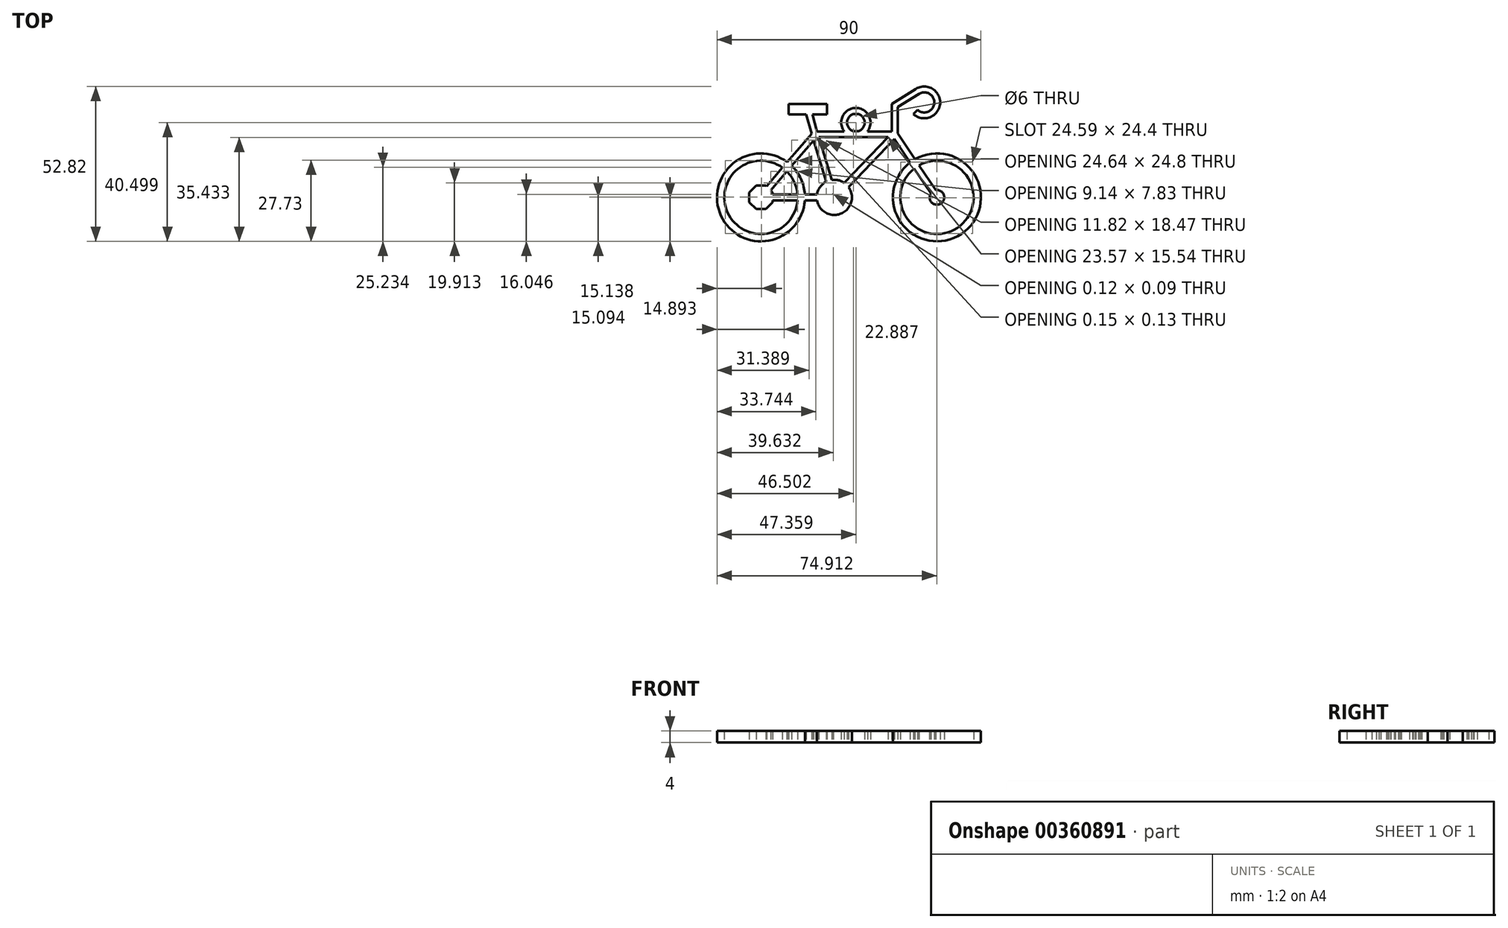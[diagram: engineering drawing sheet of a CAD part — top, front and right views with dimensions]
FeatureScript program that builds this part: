
annotation { "Feature Type Name" : "Feature", "Feature Type Description" : "" }
export const myFeature = defineFeature(function(context is Context, id is Id, definition is map)
    precondition{}
    {
        {
            var Q0;
            Q0=qCreatedBy(makeId("Top.planeOp"),FACE);
            var sketch = newSketch(context, id + "F0", { "sketchPlane" : qUnion([Q0])});
            skCircle(sketch, "E0", {"center": v(0, 0) * mm, "radius": 6 * mm});
            skCircle(sketch, "E1", {"center": v(35, 0) * mm, "radius": 2.5 * mm});
            skCircle(sketch, "E2", {"center": v(35, 0) * mm, "radius": 12.5 * mm});
            skCircle(sketch, "E3", {"center": v(35, 0) * mm, "radius": 15 * mm});
            skCircle(sketch, "E4", {"center": v(-25, 0) * mm, "radius": 12.5 * mm});
            skCircle(sketch, "E5", {"center": v(-25, 0) * mm, "radius": 15 * mm});
            skArc(sketch, "E6", {"start": v(28.35, 29.88) * mm, "mid": v(34.07, 32.08) * mm, "end": v(28.85, 35.3) * mm});
            skCircle(sketch, "E7.cCircle", {"center": v(-25, 0) * mm, "radius": 4 * mm, "construction": true});
            skLineSegment(sketch, "E7.0", {"start": v(-21, -1.66) * mm, "end": v(-23.34, -4) * mm});
            skLineSegment(sketch, "E7.1", {"start": v(-23.34, -4) * mm, "end": v(-26.66, -4) * mm});
            skLineSegment(sketch, "E7.2", {"start": v(-26.66, -4) * mm, "end": v(-29, -1.66) * mm});
            skLineSegment(sketch, "E7.3", {"start": v(-29, -1.66) * mm, "end": v(-29, 1.66) * mm});
            skLineSegment(sketch, "E7.4", {"start": v(-29, 1.66) * mm, "end": v(-26.66, 4) * mm});
            skLineSegment(sketch, "E7.5", {"start": v(-26.66, 4) * mm, "end": v(-23.34, 4) * mm});
            skLineSegment(sketch, "E7.6", {"start": v(-23.34, 4) * mm, "end": v(-21, 1.66) * mm});
            skLineSegment(sketch, "E7.7", {"start": v(-21, 1.66) * mm, "end": v(-21, -1.66) * mm});
            skPoint(sketch, "E7.0.midPoint", {"position": v(-22.17, -2.83) * mm});
            skLineSegment(sketch, "E8", {"start": v(0, 0) * mm, "end": v(-6.64, 21.5) * mm});
            skLineSegment(sketch, "E9", {"start": v(-6.64, 21.5) * mm, "end": v(-25, 0) * mm});
            skLineSegment(sketch, "E10", {"start": v(-6.64, 21.5) * mm, "end": v(20.63, 21.5) * mm});
            skLineSegment(sketch, "E11", {"start": v(20.63, 21.5) * mm, "end": v(35, 0) * mm});
            skLineSegment(sketch, "E12", {"start": v(20.63, 21.5) * mm, "end": v(0, 0) * mm});
            skLineSegment(sketch, "E13", {"start": v(-6.64, 21.5) * mm, "end": v(-9, 30.11) * mm});
            skLineSegment(sketch, "E14.bottom", {"start": v(-2.48, 28.35) * mm, "end": v(-15.52, 28.35) * mm});
            skLineSegment(sketch, "E14.top", {"start": v(-2.48, 31.87) * mm, "end": v(-15.52, 31.87) * mm});
            skLineSegment(sketch, "E14.left", {"start": v(-2.48, 28.35) * mm, "end": v(-2.48, 31.87) * mm});
            skLineSegment(sketch, "E14.right", {"start": v(-15.52, 28.35) * mm, "end": v(-15.52, 31.87) * mm});
            skPoint(sketch, "E14.middle", {"position": v(-9, 30.11) * mm});
            skLineSegment(sketch, "E15", {"start": v(20.63, 21.5) * mm, "end": v(20.63, 31.33) * mm});
            skLineSegment(sketch, "E16", {"start": v(20.63, 31.33) * mm, "end": v(28.64, 36.35) * mm});
            skArc(sketch, "E17.0", {"start": v(27, 28.4) * mm, "mid": v(35.76, 34.26) * mm, "end": v(25.28, 33.06) * mm});
            skLineSegment(sketch, "E18.0", {"start": v(19.63, 31.89) * mm, "end": v(28.1, 37.2) * mm});
            skLineSegment(sketch, "E18.1", {"start": v(19.63, 21.5) * mm, "end": v(19.63, 31.89) * mm});
            skLineSegment(sketch, "E19.0", {"start": v(19.8, 20.94) * mm, "end": v(33.87, -0.1) * mm});
            skLineSegment(sketch, "E20.0", {"start": v(19.91, 22.2) * mm, "end": v(-1.2, 0.19) * mm});
            skLineSegment(sketch, "E21.0", {"start": v(21.36, 20.8) * mm, "end": v(0.24, -1.2) * mm});
            skLineSegment(sketch, "E22.0", {"start": v(0.96, 0.3) * mm, "end": v(-5.69, 21.8) * mm});
            skLineSegment(sketch, "E23.0", {"start": v(-0.96, -0.3) * mm, "end": v(-7.6, 21.2) * mm});
            skLineSegment(sketch, "E24.0", {"start": v(-6.64, 20.5) * mm, "end": v(21.63, 20.5) * mm});
            skLineSegment(sketch, "E25.0", {"start": v(-6.64, 22.5) * mm, "end": v(21.63, 22.5) * mm});
            skLineSegment(sketch, "E26.0", {"start": v(-7.4, 22.15) * mm, "end": v(-25.76, 0.65) * mm});
            skLineSegment(sketch, "E27.0", {"start": v(-5.88, 20.85) * mm, "end": v(-24.24, -0.65) * mm});
            skLineSegment(sketch, "E28", {"start": v(-25, 0) * mm, "end": v(0, 0) * mm});
            skLineSegment(sketch, "E29.0", {"start": v(-25, -1) * mm, "end": v(0, -1) * mm});
            skLineSegment(sketch, "E30.0", {"start": v(-25, 1) * mm, "end": v(0, 1) * mm});
            skLineSegment(sketch, "E31.0", {"start": v(21.47, 22.05) * mm, "end": v(35.53, 1) * mm});
            skLineSegment(sketch, "E32.0", {"start": v(21.63, 30.78) * mm, "end": v(29.17, 35.5) * mm});
            skLineSegment(sketch, "E32.1", {"start": v(21.63, 21.5) * mm, "end": v(21.63, 30.78) * mm});
            skLineSegment(sketch, "E33.0", {"start": v(-5.68, 21.76) * mm, "end": v(-8.04, 30.37) * mm});
            skLineSegment(sketch, "E34.0", {"start": v(-7.6, 21.23) * mm, "end": v(-9.97, 29.85) * mm});
            skLineSegment(sketch, "E35", {"start": v(30.66, 32.4) * mm, "end": v(20.63, 21.5) * mm});
            skCircle(sketch, "E36", {"center": v(7.36, 25.5) * mm, "radius": 5 * mm});
            skCircle(sketch, "E37", {"center": v(7.36, 25.5) * mm, "radius": 3 * mm});
            skSolve(sketch);
        }
        {
            var Q0;
            Q0=makeQuery(id+"F0.imprint","IMPRINT",FACE,{"disambiguationData":[TD([[makeQuery(id+"F0.imprint","IMPRINT",EDGE,{"derivedFrom":sQuery(id+"F0.wireOp",EDGE,"E14.top")}),1.0]])]});
            var Q1;
            {var subQ3=sQuery(id+"F0.wireOp",EDGE,"E37");Q1=makeQuery(id+"F0.imprint","IMPRINT",FACE,{"disambiguationData":[TD([[makeQuery(id+"F0.imprint","IMPRINT",EDGE,{"derivedFrom":subQ3}),-1.0]])]});}
            var Q2;
            {var subQ0=sQuery(id+"F0.wireOp",EDGE,"E32.1");var subQ1=sQuery(id+"F0.wireOp",EDGE,"E25.0");var subQ2=makeQuery(id+"F0.imprint","INTERSECT",VERTEX,{"derivedFrom":[subQ1,subQ0]});Q2=makeQuery(id+"F0.imprint","IMPRINT",FACE,{"disambiguationData":[TD([[makeQuery(id+"F0.imprint","IMPRINT",EDGE,{"disambiguationData":[TD([[subQ2,1.0]])],"derivedFrom":subQ1}),1.0]])]});}
            var Q3;
            {var subQ0=sQuery(id+"F0.wireOp",EDGE,"E29.0");var subQ1=sQuery(id+"F0.wireOp",EDGE,"E0");var subQ2=makeQuery(id+"F0.imprint","INTERSECT",VERTEX,{"derivedFrom":[subQ1,subQ0]});Q3=makeQuery(id+"F0.imprint","IMPRINT",FACE,{"disambiguationData":[TD([[makeQuery(id+"F0.imprint","IMPRINT",EDGE,{"disambiguationData":[TD([[subQ2,1.0]])],"derivedFrom":subQ1}),-1.0]])]});}
            var Q4;
            {var subQ0=sQuery(id+"F0.wireOp",EDGE,"E31.0");var subQ1=sQuery(id+"F0.wireOp",EDGE,"E2");var subQ2=makeQuery(id+"F0.imprint","INTERSECT",VERTEX,{"derivedFrom":[subQ1,subQ0]});Q4=makeQuery(id+"F0.imprint","IMPRINT",FACE,{"disambiguationData":[TD([[makeQuery(id+"F0.imprint","IMPRINT",EDGE,{"disambiguationData":[TD([[subQ2,1.0]])],"derivedFrom":subQ1}),-1.0]])]});}
            var Q5;
            {var subQ0=sQuery(id+"F0.wireOp",EDGE,"E26.0");var subQ1=sQuery(id+"F0.wireOp",EDGE,"E4");var subQ2=makeQuery(id+"F0.imprint","INTERSECT",VERTEX,{"derivedFrom":[subQ1,subQ0]});Q5=makeQuery(id+"F0.imprint","IMPRINT",FACE,{"disambiguationData":[TD([[makeQuery(id+"F0.imprint","IMPRINT",EDGE,{"disambiguationData":[TD([[subQ2,-1.0]])],"derivedFrom":subQ1}),-1.0]])]});}
            var Q6;
            {var subQ4=sQuery(id+"F0.wireOp",EDGE,"E6");Q6=makeQuery(id+"F0.imprint","IMPRINT",FACE,{"disambiguationData":[TD([[makeQuery(id+"F0.imprint","IMPRINT",EDGE,{"derivedFrom":subQ4}),-1.0]])]});}
            var Q7;
            {var subQ1=sQuery(id+"F0.wireOp",EDGE,"E22.0");var subQ7=sQuery(id+"F0.wireOp",EDGE,"E10");var subQ8=makeQuery(id+"F0.imprint","INTERSECT",VERTEX,{"derivedFrom":[subQ7,subQ1]});Q7=makeQuery(id+"F0.imprint","IMPRINT",FACE,{"disambiguationData":[TD([[makeQuery(id+"F0.imprint","IMPRINT",EDGE,{"disambiguationData":[TD([[subQ8,-1.0]])],"derivedFrom":subQ7}),1.0]])]});}
            var Q8;
            {var subQ3=sQuery(id+"F0.wireOp",EDGE,"E16");var subQ5=sQuery(id+"F0.wireOp",EDGE,"E15");var subQ6=makeQuery(id+"F0.imprint","INTERSECT",VERTEX,{"derivedFrom":[subQ5,subQ3]});Q8=makeQuery(id+"F0.imprint","IMPRINT",FACE,{"disambiguationData":[TD([[makeQuery(id+"F0.imprint","IMPRINT",EDGE,{"disambiguationData":[TD([[subQ6,1.0]])],"derivedFrom":subQ5}),1.0]])]});}
            var Q9;
            {var subQ0=sQuery(id+"F0.wireOp",EDGE,"E21.0");var subQ1=sQuery(id+"F0.wireOp",EDGE,"E19.0");var subQ2=makeQuery(id+"F0.imprint","INTERSECT",VERTEX,{"derivedFrom":[subQ1,subQ0]});Q9=makeQuery(id+"F0.imprint","IMPRINT",FACE,{"disambiguationData":[TD([[makeQuery(id+"F0.imprint","IMPRINT",EDGE,{"disambiguationData":[TD([[subQ2,1.0]])],"derivedFrom":subQ1}),1.0]])]});}
            var Q10;
            {var subQ0=sQuery(id+"F0.wireOp",EDGE,"E21.0");var subQ6=sQuery(id+"F0.wireOp",EDGE,"E0");var subQ9=makeQuery(id+"F0.imprint","INTERSECT",VERTEX,{"derivedFrom":[subQ6,subQ0]});Q10=makeQuery(id+"F0.imprint","IMPRINT",FACE,{"disambiguationData":[TD([[makeQuery(id+"F0.imprint","IMPRINT",EDGE,{"disambiguationData":[TD([[subQ9,-1.0]])],"derivedFrom":subQ6}),-1.0]])]});}
            var Q11;
            {var subQ0=sQuery(id+"F0.wireOp",EDGE,"E11");var subQ1=sQuery(id+"F0.wireOp",EDGE,"E2");var subQ2=makeQuery(id+"F0.imprint","INTERSECT",VERTEX,{"derivedFrom":[subQ1,subQ0]});Q11=makeQuery(id+"F0.imprint","IMPRINT",FACE,{"disambiguationData":[TD([[makeQuery(id+"F0.imprint","IMPRINT",EDGE,{"disambiguationData":[TD([[subQ2,1.0]])],"derivedFrom":subQ1}),-1.0]])]});}
            var Q12;
            {var subQ0=sQuery(id+"F0.wireOp",EDGE,"E11");var subQ1=sQuery(id+"F0.wireOp",EDGE,"E2");var subQ2=makeQuery(id+"F0.imprint","INTERSECT",VERTEX,{"derivedFrom":[subQ1,subQ0]});Q12=makeQuery(id+"F0.imprint","IMPRINT",FACE,{"disambiguationData":[TD([[makeQuery(id+"F0.imprint","IMPRINT",EDGE,{"disambiguationData":[TD([[subQ2,-1.0]])],"derivedFrom":subQ1}),-1.0]])]});}
            var Q13;
            {var subQ1=sQuery(id+"F0.wireOp",EDGE,"E19.0");var subQ5=sQuery(id+"F0.wireOp",EDGE,"E3");var subQ6=makeQuery(id+"F0.imprint","INTERSECT",VERTEX,{"derivedFrom":[subQ5,subQ1]});Q13=makeQuery(id+"F0.imprint","IMPRINT",FACE,{"disambiguationData":[TD([[makeQuery(id+"F0.imprint","IMPRINT",EDGE,{"disambiguationData":[TD([[subQ6,1.0]])],"derivedFrom":subQ5}),-1.0]])]});}
            var Q14;
            {var subQ0=sQuery(id+"F0.wireOp",EDGE,"E9");var subQ1=sQuery(id+"F0.wireOp",EDGE,"E4");var subQ2=makeQuery(id+"F0.imprint","INTERSECT",VERTEX,{"derivedFrom":[subQ1,subQ0]});Q14=makeQuery(id+"F0.imprint","IMPRINT",FACE,{"disambiguationData":[TD([[makeQuery(id+"F0.imprint","IMPRINT",EDGE,{"disambiguationData":[TD([[subQ2,-1.0]])],"derivedFrom":subQ1}),-1.0]])]});}
            var Q15;
            {var subQ0=sQuery(id+"F0.wireOp",EDGE,"E28");var subQ1=sQuery(id+"F0.wireOp",EDGE,"E4");var subQ2=makeQuery(id+"F0.imprint","INTERSECT",VERTEX,{"derivedFrom":[subQ1,subQ0]});Q15=makeQuery(id+"F0.imprint","IMPRINT",FACE,{"disambiguationData":[TD([[makeQuery(id+"F0.imprint","IMPRINT",EDGE,{"disambiguationData":[TD([[subQ2,1.0]])],"derivedFrom":subQ1}),-1.0]])]});}
            var Q16;
            {var subQ0=sQuery(id+"F0.wireOp",EDGE,"E33.0");var subQ5=sQuery(id+"F0.wireOp",EDGE,"E14.bottom");var subQ6=makeQuery(id+"F0.imprint","INTERSECT",VERTEX,{"derivedFrom":[subQ5,subQ0]});Q16=makeQuery(id+"F0.imprint","IMPRINT",FACE,{"disambiguationData":[TD([[makeQuery(id+"F0.imprint","IMPRINT",EDGE,{"disambiguationData":[TD([[subQ6,-1.0]])],"derivedFrom":subQ5}),1.0]])]});}
            var Q17;
            {var subQ2=sQuery(id+"F0.wireOp",EDGE,"E36");var subQ5=sQuery(id+"F0.wireOp",EDGE,"E10");var subQ6=makeQuery(id+"F0.imprint","INTERSECT",VERTEX,{"disambiguationData":[OD(0.0)],"derivedFrom":[subQ5,subQ2]});Q17=makeQuery(id+"F0.imprint","IMPRINT",FACE,{"disambiguationData":[TD([[makeQuery(id+"F0.imprint","IMPRINT",EDGE,{"disambiguationData":[TD([[subQ6,-1.0]])],"derivedFrom":subQ5}),1.0]])]});}
            var Q18;
            {var subQ3=sQuery(id+"F0.wireOp",EDGE,"E36");var subQ7=sQuery(id+"F0.wireOp",EDGE,"E10");var subQ9=makeQuery(id+"F0.imprint","INTERSECT",VERTEX,{"disambiguationData":[OD(1.0)],"derivedFrom":[subQ7,subQ3]});Q18=makeQuery(id+"F0.imprint","IMPRINT",FACE,{"disambiguationData":[TD([[makeQuery(id+"F0.imprint","IMPRINT",EDGE,{"disambiguationData":[TD([[subQ9,-1.0]])],"derivedFrom":subQ7}),1.0]])]});}
            var Q19;
            {var subQ6=sQuery(id+"F0.wireOp",EDGE,"E5");var subQ8=sQuery(id+"F0.wireOp",EDGE,"E26.0");var subQ9=makeQuery(id+"F0.imprint","INTERSECT",VERTEX,{"derivedFrom":[subQ6,subQ8]});Q19=makeQuery(id+"F0.imprint","IMPRINT",FACE,{"disambiguationData":[TD([[makeQuery(id+"F0.imprint","IMPRINT",EDGE,{"disambiguationData":[TD([[subQ9,1.0]])],"derivedFrom":subQ6}),-1.0]])]});}
            var Q20;
            {var subQ0=sQuery(id+"F0.wireOp",EDGE,"E18.1");var subQ4=sQuery(id+"F0.wireOp",EDGE,"E10");var subQ5=makeQuery(id+"F0.imprint","INTERSECT",VERTEX,{"derivedFrom":[subQ4,subQ0]});Q20=makeQuery(id+"F0.imprint","IMPRINT",FACE,{"disambiguationData":[TD([[makeQuery(id+"F0.imprint","IMPRINT",EDGE,{"disambiguationData":[TD([[subQ5,-1.0]])],"derivedFrom":subQ0}),-1.0]])]});}
            var Q21;
            {var subQ1=sQuery(id+"F0.wireOp",EDGE,"E15");var subQ10=sQuery(id+"F0.wireOp",EDGE,"E16");var subQ12=makeQuery(id+"F0.imprint","INTERSECT",VERTEX,{"derivedFrom":[subQ1,subQ10]});Q21=makeQuery(id+"F0.imprint","IMPRINT",FACE,{"disambiguationData":[TD([[makeQuery(id+"F0.imprint","IMPRINT",EDGE,{"disambiguationData":[TD([[subQ12,1.0]])],"derivedFrom":subQ1}),-1.0]])]});}
            var Q22;
            {var subQ2=sQuery(id+"F0.wireOp",EDGE,"E0");var subQ4=makeQuery(id+"F0.imprint","INTERSECT",VERTEX,{"derivedFrom":[subQ2,sQuery(id+"F0.wireOp",EDGE,"E21.0")]});Q22=makeQuery(id+"F0.imprint","IMPRINT",FACE,{"disambiguationData":[TD([[makeQuery(id+"F0.imprint","IMPRINT",EDGE,{"disambiguationData":[TD([[subQ4,-1.0]])],"derivedFrom":subQ2}),1.0]])]});}
            var Q23;
            {var subQ9=sQuery(id+"F0.wireOp",EDGE,"E3");var subQ11=sQuery(id+"F0.wireOp",EDGE,"E31.0");var subQ13=makeQuery(id+"F0.imprint","INTERSECT",VERTEX,{"derivedFrom":[subQ9,subQ11]});Q23=makeQuery(id+"F0.imprint","IMPRINT",FACE,{"disambiguationData":[TD([[makeQuery(id+"F0.imprint","IMPRINT",EDGE,{"disambiguationData":[TD([[subQ13,-1.0]])],"derivedFrom":subQ9}),-1.0]])]});}
            var Q24;
            {var subQ0=sQuery(id+"F0.wireOp",EDGE,"E30.0");var subQ1=sQuery(id+"F0.wireOp",EDGE,"E4");var subQ2=makeQuery(id+"F0.imprint","INTERSECT",VERTEX,{"derivedFrom":[subQ1,subQ0]});Q24=makeQuery(id+"F0.imprint","IMPRINT",FACE,{"disambiguationData":[TD([[makeQuery(id+"F0.imprint","IMPRINT",EDGE,{"disambiguationData":[TD([[subQ2,-1.0]])],"derivedFrom":subQ1}),-1.0]])]});}
            var Q25;
            {var subQ0=sQuery(id+"F0.wireOp",EDGE,"E27.0");var subQ1=sQuery(id+"F0.wireOp",EDGE,"E4");var subQ2=makeQuery(id+"F0.imprint","INTERSECT",VERTEX,{"derivedFrom":[subQ1,subQ0]});Q25=makeQuery(id+"F0.imprint","IMPRINT",FACE,{"disambiguationData":[TD([[makeQuery(id+"F0.imprint","IMPRINT",EDGE,{"disambiguationData":[TD([[subQ2,-1.0]])],"derivedFrom":subQ1}),1.0]])]});}
            var Q26;
            {var subQ0=sQuery(id+"F0.wireOp",EDGE,"E9");var subQ1=sQuery(id+"F0.wireOp",EDGE,"E4");var subQ2=makeQuery(id+"F0.imprint","INTERSECT",VERTEX,{"derivedFrom":[subQ1,subQ0]});Q26=makeQuery(id+"F0.imprint","IMPRINT",FACE,{"disambiguationData":[TD([[makeQuery(id+"F0.imprint","IMPRINT",EDGE,{"disambiguationData":[TD([[subQ2,-1.0]])],"derivedFrom":subQ1}),1.0]])]});}
            var Q27;
            {var subQ5=sQuery(id+"F0.wireOp",EDGE,"E7.0");Q27=makeQuery(id+"F0.imprint","IMPRINT",FACE,{"disambiguationData":[TD([[makeQuery(id+"F0.imprint","IMPRINT",EDGE,{"derivedFrom":subQ5}),-1.0]])]});}
            var Q28;
            {var subQ0=sQuery(id+"F0.wireOp",EDGE,"E9");var subQ1=sQuery(id+"F0.wireOp",EDGE,"E7.6");var subQ2=makeQuery(id+"F0.imprint","INTERSECT",VERTEX,{"derivedFrom":[subQ1,subQ0]});Q28=makeQuery(id+"F0.imprint","IMPRINT",FACE,{"disambiguationData":[TD([[makeQuery(id+"F0.imprint","IMPRINT",EDGE,{"disambiguationData":[TD([[subQ2,-1.0]])],"derivedFrom":subQ1}),-1.0]])]});}
            var Q29;
            {var subQ0=sQuery(id+"F0.wireOp",EDGE,"E28");var subQ1=sQuery(id+"F0.wireOp",EDGE,"E9");var subQ2=makeQuery(id+"F0.imprint","INTERSECT",VERTEX,{"derivedFrom":[subQ1,subQ0]});Q29=makeQuery(id+"F0.imprint","IMPRINT",FACE,{"disambiguationData":[TD([[makeQuery(id+"F0.imprint","IMPRINT",EDGE,{"disambiguationData":[TD([[subQ2,1.0]])],"derivedFrom":subQ1}),1.0]])]});}
            var Q30;
            {var subQ0=sQuery(id+"F0.wireOp",EDGE,"E30.0");var subQ1=sQuery(id+"F0.wireOp",EDGE,"E7.7");var subQ2=makeQuery(id+"F0.imprint","INTERSECT",VERTEX,{"derivedFrom":[subQ1,subQ0]});Q30=makeQuery(id+"F0.imprint","IMPRINT",FACE,{"disambiguationData":[TD([[makeQuery(id+"F0.imprint","IMPRINT",EDGE,{"disambiguationData":[TD([[subQ2,-1.0]])],"derivedFrom":subQ1}),-1.0]])]});}
            var Q31;
            {var subQ0=sQuery(id+"F0.wireOp",EDGE,"E30.0");var subQ1=sQuery(id+"F0.wireOp",EDGE,"E4");var subQ2=makeQuery(id+"F0.imprint","INTERSECT",VERTEX,{"derivedFrom":[subQ1,subQ0]});Q31=makeQuery(id+"F0.imprint","IMPRINT",FACE,{"disambiguationData":[TD([[makeQuery(id+"F0.imprint","IMPRINT",EDGE,{"disambiguationData":[TD([[subQ2,1.0]])],"derivedFrom":subQ1}),1.0]])]});}
            var Q32;
            {var subQ0=sQuery(id+"F0.wireOp",EDGE,"E28");var subQ1=sQuery(id+"F0.wireOp",EDGE,"E4");var subQ2=makeQuery(id+"F0.imprint","INTERSECT",VERTEX,{"derivedFrom":[subQ1,subQ0]});Q32=makeQuery(id+"F0.imprint","IMPRINT",FACE,{"disambiguationData":[TD([[makeQuery(id+"F0.imprint","IMPRINT",EDGE,{"disambiguationData":[TD([[subQ2,1.0]])],"derivedFrom":subQ1}),1.0]])]});}
            var Q33;
            {var subQ0=sQuery(id+"F0.wireOp",EDGE,"E23.0");var subQ1=sQuery(id+"F0.wireOp",EDGE,"E0");var subQ2=makeQuery(id+"F0.imprint","INTERSECT",VERTEX,{"derivedFrom":[subQ1,subQ0]});Q33=makeQuery(id+"F0.imprint","IMPRINT",FACE,{"disambiguationData":[TD([[makeQuery(id+"F0.imprint","IMPRINT",EDGE,{"disambiguationData":[TD([[subQ2,-1.0]])],"derivedFrom":subQ1}),1.0]])]});}
            var Q34;
            {var subQ2=sQuery(id+"F0.wireOp",EDGE,"E30.0");var subQ4=sQuery(id+"F0.wireOp",EDGE,"E0");var subQ5=makeQuery(id+"F0.imprint","INTERSECT",VERTEX,{"derivedFrom":[subQ4,subQ2]});Q34=makeQuery(id+"F0.imprint","IMPRINT",FACE,{"disambiguationData":[TD([[makeQuery(id+"F0.imprint","IMPRINT",EDGE,{"disambiguationData":[TD([[subQ5,-1.0]])],"derivedFrom":subQ4}),1.0]])]});}
            var Q35;
            {var subQ0=sQuery(id+"F0.wireOp",EDGE,"E30.0");var subQ1=sQuery(id+"F0.wireOp",EDGE,"E0");var subQ2=makeQuery(id+"F0.imprint","INTERSECT",VERTEX,{"derivedFrom":[subQ1,subQ0]});Q35=makeQuery(id+"F0.imprint","IMPRINT",FACE,{"disambiguationData":[TD([[makeQuery(id+"F0.imprint","IMPRINT",EDGE,{"disambiguationData":[TD([[subQ2,-1.0]])],"derivedFrom":subQ1}),-1.0]])]});}
            var Q36;
            {var subQ0=sQuery(id+"F0.wireOp",EDGE,"E30.0");var subQ1=sQuery(id+"F0.wireOp",EDGE,"E4");var subQ2=makeQuery(id+"F0.imprint","INTERSECT",VERTEX,{"derivedFrom":[subQ1,subQ0]});Q36=makeQuery(id+"F0.imprint","IMPRINT",FACE,{"disambiguationData":[TD([[makeQuery(id+"F0.imprint","IMPRINT",EDGE,{"disambiguationData":[TD([[subQ2,1.0]])],"derivedFrom":subQ1}),-1.0]])]});}
            var Q37;
            {var subQ0=sQuery(id+"F0.wireOp",EDGE,"E20.0");var subQ1=sQuery(id+"F0.wireOp",EDGE,"E0");var subQ2=makeQuery(id+"F0.imprint","INTERSECT",VERTEX,{"derivedFrom":[subQ1,subQ0]});Q37=makeQuery(id+"F0.imprint","IMPRINT",FACE,{"disambiguationData":[TD([[makeQuery(id+"F0.imprint","IMPRINT",EDGE,{"disambiguationData":[TD([[subQ2,-1.0]])],"derivedFrom":subQ1}),1.0]])]});}
            var Q38;
            {var subQ0=sQuery(id+"F0.wireOp",EDGE,"E22.0");var subQ1=sQuery(id+"F0.wireOp",EDGE,"E0");var subQ2=makeQuery(id+"F0.imprint","INTERSECT",VERTEX,{"derivedFrom":[subQ1,subQ0]});Q38=makeQuery(id+"F0.imprint","IMPRINT",FACE,{"disambiguationData":[TD([[makeQuery(id+"F0.imprint","IMPRINT",EDGE,{"disambiguationData":[TD([[subQ2,-1.0]])],"derivedFrom":subQ1}),1.0]])]});}
            var Q39;
            {var subQ1=sQuery(id+"F0.wireOp",EDGE,"E0");var subQ5=sQuery(id+"F0.wireOp",EDGE,"E8");var subQ6=makeQuery(id+"F0.imprint","INTERSECT",VERTEX,{"derivedFrom":[subQ1,subQ5]});Q39=makeQuery(id+"F0.imprint","IMPRINT",FACE,{"disambiguationData":[TD([[makeQuery(id+"F0.imprint","IMPRINT",EDGE,{"disambiguationData":[TD([[subQ6,-1.0]])],"derivedFrom":subQ1}),1.0]])]});}
            var Q40;
            {var subQ0=sQuery(id+"F0.wireOp",EDGE,"E12");var subQ1=sQuery(id+"F0.wireOp",EDGE,"E0");var subQ2=makeQuery(id+"F0.imprint","INTERSECT",VERTEX,{"derivedFrom":[subQ1,subQ0]});Q40=makeQuery(id+"F0.imprint","IMPRINT",FACE,{"disambiguationData":[TD([[makeQuery(id+"F0.imprint","IMPRINT",EDGE,{"disambiguationData":[TD([[subQ2,-1.0]])],"derivedFrom":subQ1}),1.0]])]});}
            var Q41;
            {var subQ0=sQuery(id+"F0.wireOp",EDGE,"E12");var subQ1=sQuery(id+"F0.wireOp",EDGE,"E0");var subQ2=makeQuery(id+"F0.imprint","INTERSECT",VERTEX,{"derivedFrom":[subQ1,subQ0]});Q41=makeQuery(id+"F0.imprint","IMPRINT",FACE,{"disambiguationData":[TD([[makeQuery(id+"F0.imprint","IMPRINT",EDGE,{"disambiguationData":[TD([[subQ2,-1.0]])],"derivedFrom":subQ1}),-1.0]])]});}
            var Q42;
            {var subQ0=sQuery(id+"F0.wireOp",EDGE,"E27.0");var subQ1=sQuery(id+"F0.wireOp",EDGE,"E5");var subQ2=makeQuery(id+"F0.imprint","INTERSECT",VERTEX,{"derivedFrom":[subQ1,subQ0]});Q42=makeQuery(id+"F0.imprint","IMPRINT",FACE,{"disambiguationData":[TD([[makeQuery(id+"F0.imprint","IMPRINT",EDGE,{"disambiguationData":[TD([[subQ2,-1.0]])],"derivedFrom":subQ1}),-1.0]])]});}
            var Q43;
            {var subQ0=sQuery(id+"F0.wireOp",EDGE,"E27.0");var subQ1=sQuery(id+"F0.wireOp",EDGE,"E4");var subQ2=makeQuery(id+"F0.imprint","INTERSECT",VERTEX,{"derivedFrom":[subQ1,subQ0]});Q43=makeQuery(id+"F0.imprint","IMPRINT",FACE,{"disambiguationData":[TD([[makeQuery(id+"F0.imprint","IMPRINT",EDGE,{"disambiguationData":[TD([[subQ2,-1.0]])],"derivedFrom":subQ1}),-1.0]])]});}
            var Q44;
            {var subQ4=sQuery(id+"F0.wireOp",EDGE,"E10");var subQ6=sQuery(id+"F0.wireOp",EDGE,"E22.0");var subQ7=makeQuery(id+"F0.imprint","INTERSECT",VERTEX,{"derivedFrom":[subQ4,subQ6]});Q44=makeQuery(id+"F0.imprint","IMPRINT",FACE,{"disambiguationData":[TD([[makeQuery(id+"F0.imprint","IMPRINT",EDGE,{"disambiguationData":[TD([[subQ7,1.0]])],"derivedFrom":subQ6}),1.0]])]});}
            var Q45;
            {var subQ1=sQuery(id+"F0.wireOp",EDGE,"E8");var subQ7=makeQuery(id+"F0.imprint","INTERSECT",VERTEX,{"derivedFrom":[subQ1,sQuery(id+"F0.wireOp",EDGE,"E24.0")]});Q45=makeQuery(id+"F0.imprint","IMPRINT",FACE,{"disambiguationData":[TD([[makeQuery(id+"F0.imprint","IMPRINT",EDGE,{"disambiguationData":[TD([[subQ7,1.0]])],"derivedFrom":subQ1}),1.0]])]});}
            var Q46;
            {var subQ0=sQuery(id+"F0.wireOp",EDGE,"E22.0");var subQ1=sQuery(id+"F0.wireOp",EDGE,"E10");var subQ2=makeQuery(id+"F0.imprint","INTERSECT",VERTEX,{"derivedFrom":[subQ1,subQ0]});Q46=makeQuery(id+"F0.imprint","IMPRINT",FACE,{"disambiguationData":[TD([[makeQuery(id+"F0.imprint","IMPRINT",EDGE,{"disambiguationData":[TD([[subQ2,-1.0]])],"derivedFrom":subQ1}),-1.0]])]});}
            var Q47;
            {var subQ4=sQuery(id+"F0.wireOp",EDGE,"E10");var subQ6=makeQuery(id+"F0.imprint","INTERSECT",VERTEX,{"derivedFrom":[subQ4,sQuery(id+"F0.wireOp",EDGE,"E18.1")]});Q47=makeQuery(id+"F0.imprint","IMPRINT",FACE,{"disambiguationData":[TD([[makeQuery(id+"F0.imprint","IMPRINT",EDGE,{"disambiguationData":[TD([[subQ6,1.0]])],"derivedFrom":subQ4}),-1.0]])]});}
            var Q48;
            {var subQ0=sQuery(id+"F0.wireOp",EDGE,"E19.0");var subQ1=sQuery(id+"F0.wireOp",EDGE,"E12");var subQ2=makeQuery(id+"F0.imprint","INTERSECT",VERTEX,{"derivedFrom":[subQ1,subQ0]});Q48=makeQuery(id+"F0.imprint","IMPRINT",FACE,{"disambiguationData":[TD([[makeQuery(id+"F0.imprint","IMPRINT",EDGE,{"disambiguationData":[TD([[subQ2,-1.0]])],"derivedFrom":subQ0}),1.0]])]});}
            var Q49;
            {var subQ0=sQuery(id+"F0.wireOp",EDGE,"E21.0");var subQ1=sQuery(id+"F0.wireOp",EDGE,"E11");var subQ2=makeQuery(id+"F0.imprint","INTERSECT",VERTEX,{"derivedFrom":[subQ1,subQ0]});Q49=makeQuery(id+"F0.imprint","IMPRINT",FACE,{"disambiguationData":[TD([[makeQuery(id+"F0.imprint","IMPRINT",EDGE,{"disambiguationData":[TD([[subQ2,-1.0]])],"derivedFrom":subQ1}),-1.0]])]});}
            var Q50;
            {var subQ0=sQuery(id+"F0.wireOp",EDGE,"E19.0");var subQ1=sQuery(id+"F0.wireOp",EDGE,"E12");var subQ2=makeQuery(id+"F0.imprint","INTERSECT",VERTEX,{"derivedFrom":[subQ1,subQ0]});Q50=makeQuery(id+"F0.imprint","IMPRINT",FACE,{"disambiguationData":[TD([[makeQuery(id+"F0.imprint","IMPRINT",EDGE,{"disambiguationData":[TD([[subQ2,-1.0]])],"derivedFrom":subQ1}),1.0]])]});}
            var Q51;
            {var subQ0=sQuery(id+"F0.wireOp",EDGE,"E18.1");var subQ1=sQuery(id+"F0.wireOp",EDGE,"E10");var subQ2=makeQuery(id+"F0.imprint","INTERSECT",VERTEX,{"derivedFrom":[subQ1,subQ0]});Q51=makeQuery(id+"F0.imprint","IMPRINT",FACE,{"disambiguationData":[TD([[makeQuery(id+"F0.imprint","IMPRINT",EDGE,{"disambiguationData":[TD([[subQ2,1.0]])],"derivedFrom":subQ1}),1.0]])]});}
            var Q52;
            {var subQ0=sQuery(id+"F0.wireOp",EDGE,"E23.0");var subQ1=sQuery(id+"F0.wireOp",EDGE,"E20.0");var subQ2=makeQuery(id+"F0.imprint","INTERSECT",VERTEX,{"derivedFrom":[subQ1,subQ0]});Q52=makeQuery(id+"F0.imprint","IMPRINT",FACE,{"disambiguationData":[TD([[makeQuery(id+"F0.imprint","IMPRINT",EDGE,{"disambiguationData":[TD([[subQ2,1.0]])],"derivedFrom":subQ1}),-1.0]])]});}
            var Q53;
            {var subQ0=sQuery(id+"F0.wireOp",EDGE,"E23.0");var subQ1=sQuery(id+"F0.wireOp",EDGE,"E20.0");var subQ2=makeQuery(id+"F0.imprint","INTERSECT",VERTEX,{"derivedFrom":[subQ1,subQ0]});Q53=makeQuery(id+"F0.imprint","IMPRINT",FACE,{"disambiguationData":[TD([[makeQuery(id+"F0.imprint","IMPRINT",EDGE,{"disambiguationData":[TD([[subQ2,1.0]])],"derivedFrom":subQ1}),1.0]])]});}
            var Q54;
            {var subQ1=sQuery(id+"F0.wireOp",EDGE,"E8");var subQ5=makeQuery(id+"F0.imprint","INTERSECT",VERTEX,{"derivedFrom":[subQ1,sQuery(id+"F0.wireOp",EDGE,"E30.0")]});Q54=makeQuery(id+"F0.imprint","IMPRINT",FACE,{"disambiguationData":[TD([[makeQuery(id+"F0.imprint","IMPRINT",EDGE,{"disambiguationData":[TD([[subQ5,-1.0]])],"derivedFrom":subQ1}),-1.0]])]});}
            var Q55;
            {var subQ0=sQuery(id+"F0.wireOp",EDGE,"E7.7");var subQ1=sQuery(id+"F0.wireOp",EDGE,"E7.6");var subQ2=makeQuery(id+"F0.imprint","INTERSECT",VERTEX,{"derivedFrom":[subQ1,subQ0]});Q55=makeQuery(id+"F0.imprint","IMPRINT",FACE,{"disambiguationData":[TD([[makeQuery(id+"F0.imprint","IMPRINT",EDGE,{"disambiguationData":[TD([[subQ2,1.0]])],"derivedFrom":subQ1}),-1.0]])]});}
            var Q56;
            {var subQ0=sQuery(id+"F0.wireOp",EDGE,"E11");var subQ1=sQuery(id+"F0.wireOp",EDGE,"E1");var subQ2=makeQuery(id+"F0.imprint","INTERSECT",VERTEX,{"derivedFrom":[subQ1,subQ0]});Q56=makeQuery(id+"F0.imprint","IMPRINT",FACE,{"disambiguationData":[TD([[makeQuery(id+"F0.imprint","IMPRINT",EDGE,{"disambiguationData":[TD([[subQ2,1.0]])],"derivedFrom":subQ1}),-1.0]])]});}
            var Q57;
            {var subQ0=sQuery(id+"F0.wireOp",EDGE,"E11");var subQ1=sQuery(id+"F0.wireOp",EDGE,"E1");var subQ2=makeQuery(id+"F0.imprint","INTERSECT",VERTEX,{"derivedFrom":[subQ1,subQ0]});Q57=makeQuery(id+"F0.imprint","IMPRINT",FACE,{"disambiguationData":[TD([[makeQuery(id+"F0.imprint","IMPRINT",EDGE,{"disambiguationData":[TD([[subQ2,-1.0]])],"derivedFrom":subQ1}),-1.0]])]});}
            var Q58;
            {var subQ0=sQuery(id+"F0.wireOp",EDGE,"E1");var subQ1=makeQuery(id+"F0.imprint","INTERSECT",VERTEX,{"derivedFrom":[subQ0,sQuery(id+"F0.wireOp",EDGE,"E11")]});Q58=makeQuery(id+"F0.imprint","IMPRINT",FACE,{"disambiguationData":[TD([[makeQuery(id+"F0.imprint","IMPRINT",EDGE,{"disambiguationData":[TD([[subQ1,1.0]])],"derivedFrom":subQ0}),1.0]])]});}
            var Q59;
            {var subQ0=sQuery(id+"F0.wireOp",EDGE,"E8");var subQ1=sQuery(id+"F0.wireOp",EDGE,"E0");var subQ2=makeQuery(id+"F0.imprint","INTERSECT",VERTEX,{"derivedFrom":[subQ1,subQ0]});Q59=makeQuery(id+"F0.imprint","IMPRINT",FACE,{"disambiguationData":[TD([[makeQuery(id+"F0.imprint","IMPRINT",EDGE,{"disambiguationData":[TD([[subQ2,-1.0]])],"derivedFrom":subQ1}),-1.0]])]});}
            var Q60;
            {var subQ3=sQuery(id+"F0.wireOp",EDGE,"E22.0");var subQ5=sQuery(id+"F0.wireOp",EDGE,"E0");var subQ6=makeQuery(id+"F0.imprint","INTERSECT",VERTEX,{"derivedFrom":[subQ5,subQ3]});Q60=makeQuery(id+"F0.imprint","IMPRINT",FACE,{"disambiguationData":[TD([[makeQuery(id+"F0.imprint","IMPRINT",EDGE,{"disambiguationData":[TD([[subQ6,-1.0]])],"derivedFrom":subQ5}),-1.0]])]});}
            var Q61;
            {var subQ0=sQuery(id+"F0.wireOp",EDGE,"E36");var subQ1=sQuery(id+"F0.wireOp",EDGE,"E10");var subQ2=makeQuery(id+"F0.imprint","INTERSECT",VERTEX,{"disambiguationData":[OD(0.0)],"derivedFrom":[subQ1,subQ0]});Q61=makeQuery(id+"F0.imprint","IMPRINT",FACE,{"disambiguationData":[TD([[makeQuery(id+"F0.imprint","IMPRINT",EDGE,{"disambiguationData":[TD([[subQ2,-1.0]])],"derivedFrom":subQ1}),-1.0]])]});}
            var Q62;
            {var subQ0=sQuery(id+"F0.wireOp",EDGE,"E36");var subQ1=sQuery(id+"F0.wireOp",EDGE,"E10");var subQ2=makeQuery(id+"F0.imprint","INTERSECT",VERTEX,{"disambiguationData":[OD(1.0)],"derivedFrom":[subQ1,subQ0]});Q62=makeQuery(id+"F0.imprint","IMPRINT",FACE,{"disambiguationData":[TD([[makeQuery(id+"F0.imprint","IMPRINT",EDGE,{"disambiguationData":[TD([[subQ2,-1.0]])],"derivedFrom":subQ1}),-1.0]])]});}
            var Q63;
            {var subQ1=sQuery(id+"F0.wireOp",EDGE,"E15");var subQ3=sQuery(id+"F0.wireOp",EDGE,"E25.0");var subQ4=makeQuery(id+"F0.imprint","INTERSECT",VERTEX,{"derivedFrom":[subQ1,subQ3]});Q63=makeQuery(id+"F0.imprint","IMPRINT",FACE,{"disambiguationData":[TD([[makeQuery(id+"F0.imprint","IMPRINT",EDGE,{"disambiguationData":[TD([[subQ4,-1.0]])],"derivedFrom":subQ3}),-1.0]])]});}
            extrude(context, id + "F1", {"entities" : qUnion([Q0, Q1, Q2, Q3, Q4, Q5, Q6, Q7, Q8, Q9, Q10, Q11, Q12, Q13, Q14, Q15, Q16, Q17, Q18, Q19, Q20, Q21, Q22, Q23, Q24, Q25, Q26, Q27, Q28, Q29, Q30, Q31, Q32, Q33, Q34, Q35, Q36, Q37, Q38, Q39, Q40, Q41, Q42, Q43, Q44, Q45, Q46, Q47, Q48, Q49, Q50, Q51, Q52, Q53, Q54, Q55, Q56, Q57, Q58, Q59, Q60, Q61, Q62, Q63]), "depth" : 4 * mm});
        }
    });
